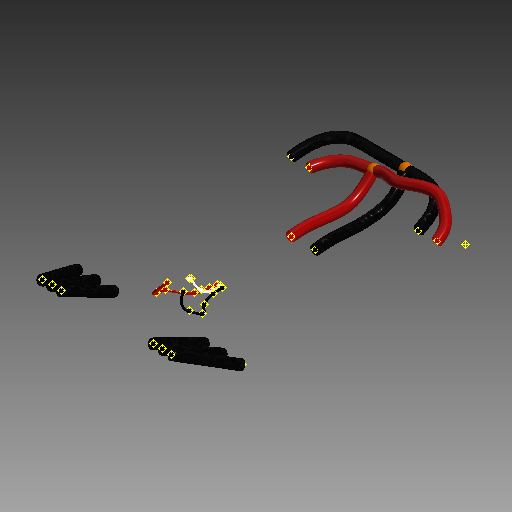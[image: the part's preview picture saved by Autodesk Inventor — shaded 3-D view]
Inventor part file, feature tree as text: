
AUTODESK INVENTOR PART (.ipt)
format: ipt  version: 2019.2 (Build 232265000, 265)  size: 1,440,768 bytes
history: native  units: mm (DEFAULTED — no unit token found)
features: other x108, sketch x29, plane x27, sweep x27, revolve x2
ambient origin geometry x8: Origin, YZ Plane, XZ Plane, XY Plane, X Axis, Y Axis, Z Axis, Center Point
bodies: Body1 (feature_tree), Body2 (feature_tree), Body3 (feature_tree), Body4 (feature_tree), Body5 (feature_tree), Body6 (feature_tree), Body7 (feature_tree), Body8 (feature_tree), Body9 (feature_tree), Body10 (feature_tree), Body11 (feature_tree), Body12 (feature_tree), Body13 (feature_tree), Body14 (feature_tree), Body15 (feature_tree), Body16 (feature_tree), Body17 (feature_tree), Body18 (feature_tree), Body19 (feature_tree), Body20 (feature_tree), Body21 (feature_tree), Body22 (feature_tree), Body23 (feature_tree), Body24 (feature_tree), Body25 (feature_tree), Body26 (feature_tree), Body27 (feature_tree), Body28 (feature_tree), Body29 (feature_tree)
feature tree (193):
  other  "Work Point3"
  other  "Work Point4"
  other  "n_vesc"
  other  "Work Point12"
  other  "Work Point13"
  other  "p_vesc"
  other  "Work Point20"
  other  "Work Point21"
  other  "n_out"
  other  "Work Point28"
  other  "Work Point29"
  other  "p_out"
  other  "Work Point30"
  other  "Work Point37"
  other  "Work Point38"
  other  "m1_3"
  other  "Work Point39"
  other  "Work Point40"
  other  "m1_2"
  other  "Work Point41"
  other  "Work Point42"
  other  "m1_1"
  other  "Work Point43"
  other  "Work Point44"
  other  "m2_3"
  other  "Work Point45"
  other  "Work Point46"
  other  "m2_2"
  other  "Work Point47"
  other  "Work Point48"
  other  "m2_1"
  plane  "Work Plane21"
  plane  "Work Plane22"
  plane  "Work Plane23"
  plane  "Work Plane24"
  plane  "Work Plane25"
  plane  "Work Plane26"
  other  "Work Point49"
  other  "Segment1"
  other  "Work Point51"
  plane  "Work Plane37"
  plane  "Work Plane38"
  other  "Work Point52"
  other  "Work Point53"
  other  "Segment2"
  other  "Work Point54"
  other  "Work Point55"
  other  "Work Point56"
  plane  "Work Plane40"
  plane  "Work Plane41"
  other  "Work Point58"
  other  "Work Point59"
  other  "Work Point60"
  other  "Segment2_1"
  plane  "Work Plane42"
  plane  "Work Plane43"
  other  "Work Point61"
  other  "Segment3"
  other  "Work Point62"
  plane  "Work Plane44"
  plane  "Work Plane45"
  other  "Work Point63"
  other  "Work Point65"
  other  "Work Point66"
  other  "Work Point67"
  other  "Segment1_1"
  plane  "Work Plane46"
  plane  "Work Plane47"
  other  "Work Point68"
  other  "Segment4"
  other  "Work Point69"
  plane  "Work Plane48"
  other  "Work Point70"
  plane  "Work Plane49"
  other  "Work Point77"
  other  "Work Point78"
  other  "Segment5"
  other  "Work Point79"
  other  "Work Point80"
  plane  "Work Plane53"
  other  "Work Point81"
  other  "Work Point82"
  other  "Segment6"
  other  "Work Point83"
  other  "Work Point84"
  plane  "Work Plane56"
  other  "Work Point85"
  other  "Work Point86"
  other  "Segment7"
  other  "Work Point87"
  plane  "Work Plane59"
  other  "Work Point88"
  other  "Work Point89"
  other  "Wire1"
  other  "Work Point90"
  other  "Work Point91"
  other  "Wire2"
  other  "Work Point92"
  other  "Work Point93"
  other  "Wire3"
  plane  "Work Plane62"
  plane  "Work Plane63"
  plane  "Work Plane64"
  plane  "Work Plane65"
  plane  "Work Plane66"
  plane  "Work Plane67"
  sketch  "Sketch23"  dims[d38=0.0mm d39=0.0mm d40=0.0mm d41=0.0mm]
  other  "Srf21"
  sketch  "Sketch24"  dims[d42=0.0mm d43=0.0mm d44=0.0mm d45=0.0mm]
  other  "Srf22"
  sketch  "Sketch25"  dims[d46=0.0mm d47=0.0mm d48=0.0mm d49=0.0mm]
  other  "Srf23"
  sketch  "Sketch26"  dims[d68=0.0mm d69=0.0mm d70=0.0mm d71=0.0mm]
  other  "Srf24"
  sketch  "Sketch27"  dims[d74=0.0mm d75=0.0mm d76=0.0mm d77=0.0mm]
  other  "Srf25"
  sketch  "Sketch28"  dims[d78=0.0mm d79=0.0mm d80=0.0mm d81=0.0mm]
  other  "Srf26"
  sketch  "Sketch39"  dims[d82=0.0mm d83=0.0mm d84=0.0mm]
  other  "Srf36"
  sketch  "Sketch40"  dims[d85=0.0mm d86=0.0mm d87=0.0mm d88=0.0mm]
  other  "Srf37"
  sketch  "Sketch42"  dims[d89=0.0mm d90=0.0mm d91=0.0mm]
  other  "Srf39"
  sketch  "Sketch43"  dims[d92=0.0mm d93=0.0mm d94=0.0mm d95=0.0mm]
  other  "Srf40"
  sketch  "Sketch44"  dims[d102=0.0mm d103=0.0mm d108=0.0mm d109=0.0mm]
  other  "Srf41"
  sketch  "Sketch45"  dims[d114=0.0mm d115=0.0mm d120=0.0mm d121=0.0mm]
  other  "Srf42"
  sketch  "Sketch46"  dims[d122=0.0mm d123=0.0mm d124=0.0mm d125=0.0mm]
  other  "Srf43"
  sketch  "Sketch47"  dims[d126=0.0mm d127=0.0mm d128=0.0mm d129=0.0mm]
  other  "Srf44"
  sketch  "Sketch48"  dims[d130=0.0mm d131=0.0mm]
  other  "Srf45"
  sketch  "Sketch49"
  other  "Srf46"
  sketch  "Sketch50"
  other  "Srf47"
  sketch  "Sketch51"
  other  "Srf48"
  sketch  "Sketch52"
  other  "Srf49"
  sketch  "Sketch53"
  other  "Srf50"
  sketch  "Sketch57"
  other  "Srf54"
  sketch  "Sketch60"
  other  "Srf57"
  sketch  "Sketch63"
  other  "Srf60"
  sketch  "Sketch66"
  other  "Srf63"
  sketch  "Sketch67"
  other  "Srf64"
  sketch  "Sketch68"
  other  "Srf65"
  sketch  "Sketch69"
  other  "Srf66"
  sketch  "Sketch70"
  other  "Srf67"
  sketch  "Sketch71"
  other  "Srf68"
  sweep  "SweepSrf19"
  sweep  "SweepSrf20"
  sweep  "SweepSrf21"
  sweep  "SweepSrf22"
  sweep  "SweepSrf23"
  sweep  "SweepSrf24"
  sweep  "SweepSrf34"
  sweep  "SweepSrf35"
  sweep  "SweepSrf37"
  sweep  "SweepSrf38"
  sweep  "SweepSrf39"
  sweep  "SweepSrf40"
  revolve  "RevolutionSrf3"  [1 undecoded]
  sweep  "SweepSrf41"
  sweep  "SweepSrf42"
  sweep  "SweepSrf43"
  sweep  "SweepSrf44"
  revolve  "RevolutionSrf4"  [1 undecoded]
  sweep  "SweepSrf45"
  sweep  "SweepSrf46"
  sweep  "SweepSrf50"
  sweep  "SweepSrf53"
  sweep  "SweepSrf56"
  sweep  "SweepSrf59"
  sweep  "SweepSrf60"
  sweep  "SweepSrf61"
  sweep  "SweepSrf62"
  sweep  "SweepSrf63"
  sweep  "SweepSrf64"
note: 2 required parameter values undecoded (feature->parameter linkage not recoverable at this tier; creation-order binding heuristic only, values carry confidence <= 0.55)